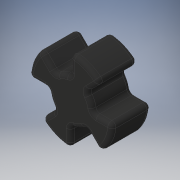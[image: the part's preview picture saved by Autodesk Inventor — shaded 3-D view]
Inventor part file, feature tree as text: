
AUTODESK INVENTOR PART (.ipt)
format: ipt  version: 2018 (Build 220112000, 112)  size: 295,424 bytes
history: native  units: in
note: dims shown in document units (in); Inventor stores cm internally (conversion verified against a paired STEP export)
features: fillet x2, extrude x1, pattern_circular x1, sketch x1
ambient origin geometry x8: Origin, YZ Plane, XZ Plane, XY Plane, X Axis, Y Axis, Z Axis, Center Point
bodies: Body1 (feature_tree)
feature tree (5):
  extrude  "Extrusion3"  TaperAngle=45.0deg  [1 undecoded]
  fillet  "Fillet3"  Radius=0.325in
  pattern_circular  "Circular Pattern2"  [2 undecoded]
  fillet  "Fillet4"  Radius=0.0312in
  sketch  "Sketch1"  dims[d0=0.625in d2=45.0deg d13=0.325in d14=0.2936in d15=0.0in d16=0.0312in d17=1.5748in d18=360.0deg d20=0.0312in]
note: 3 required parameter values undecoded (feature->parameter linkage not recoverable at this tier; creation-order binding heuristic only, values carry confidence <= 0.55)
